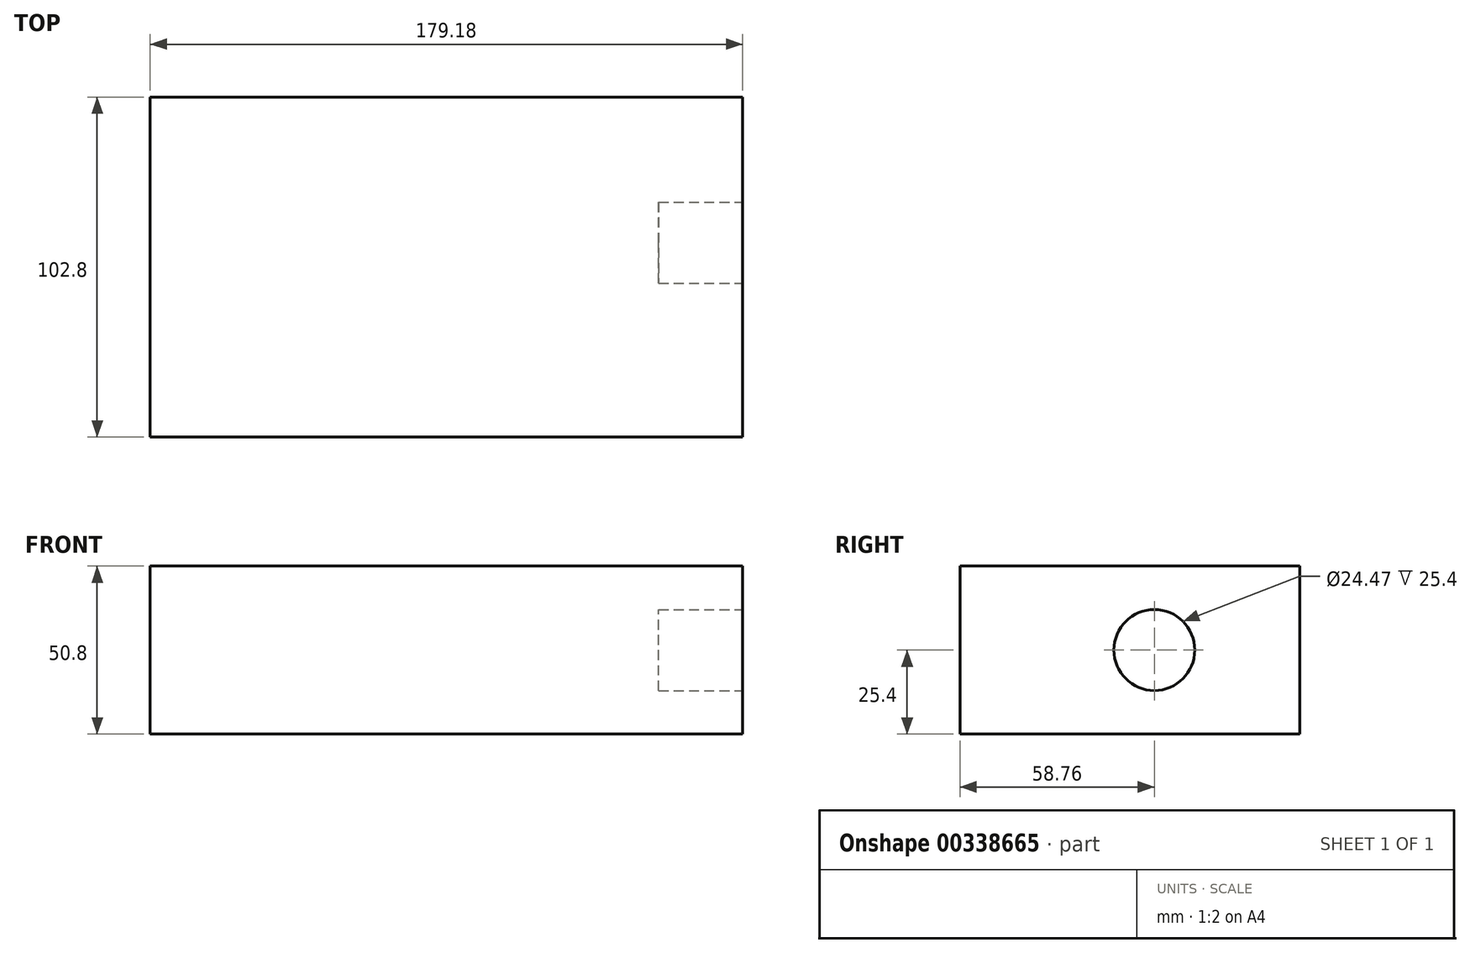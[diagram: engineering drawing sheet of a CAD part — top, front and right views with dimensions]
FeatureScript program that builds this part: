
annotation { "Feature Type Name" : "Feature", "Feature Type Description" : "" }
export const myFeature = defineFeature(function(context is Context, id is Id, definition is map)
    precondition{}
    {
        {
            var Q0;
            Q0=qCreatedBy(makeId("Top.planeOp"),FACE);
            var sketch = newSketch(context, id + "F0", { "sketchPlane" : qUnion([Q0])});
            skLineSegment(sketch, "E0.bottom", {"start": v(-89.59, 51.4) * mm, "end": v(89.59, 51.4) * mm});
            skLineSegment(sketch, "E0.top", {"start": v(-89.59, -51.4) * mm, "end": v(89.59, -51.4) * mm});
            skLineSegment(sketch, "E0.left", {"start": v(-89.59, 51.4) * mm, "end": v(-89.59, -51.4) * mm});
            skLineSegment(sketch, "E0.right", {"start": v(89.59, 51.4) * mm, "end": v(89.59, -51.4) * mm});
            skPoint(sketch, "E0.middle", {"position": v(0, 0) * mm});
            skSolve(sketch);
        }
        {
            var Q0;
            Q0 = qSketchRegion(id + "F0", true);
            extrude(context, id + "F1", {"entities" : qUnion([Q0]), "depth" : 50.8 * mm});
        }
        {
            var Q0;
            Q0=makeQuery(id+"F1.opExtrude","SWEPT_FACE",FACE,{"disambiguationData":[OSD([sQuery(id+"F0.wireOp",EDGE,"E0.right")])]});
            var sketch = newSketch(context, id + "F2", { "sketchPlane" : qUnion([Q0])});
            skCircle(sketch, "E1", {"center": v(7.36, 25.4) * mm, "radius": 12.23 * mm});
            skPoint(sketch, "E1.centerSnap0", {"position": v(-51.4, 25.4) * mm});
            skSolve(sketch);
        }
        {
            var Q0;
            Q0=makeQuery(id+"F2.imprint","IMPRINT",FACE,{"disambiguationData":[TD([[makeQuery(id+"F2.imprint","IMPRINT",EDGE,{"derivedFrom":sQuery(id+"F2.wireOp",EDGE,"E1")}),1.0]])]});
            var Q1;
            Q1=sQuery(id+"F2.wireOp",EDGE,"E1");
            extrude(context, id + "F3", {"entities" : qUnion([Q0]), "operationType" : NewBodyOperationType.REMOVE, "surfaceEntities" : qUnion([Q1]), "oppositeDirection" : true, "depth" : 25.4 * mm});
        }
    });
